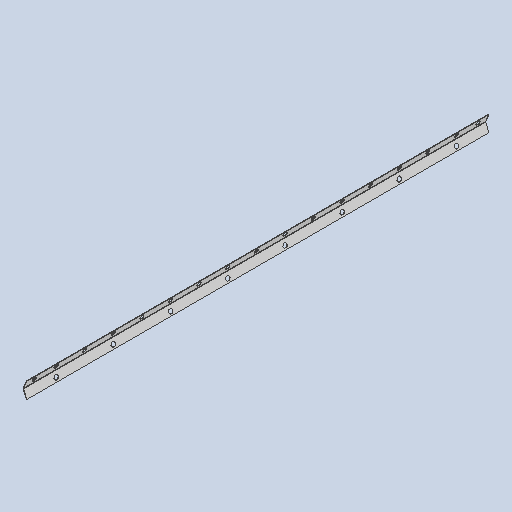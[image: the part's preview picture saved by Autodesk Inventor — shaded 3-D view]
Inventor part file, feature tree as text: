
AUTODESK INVENTOR PART (.ipt)
format: ipt  version: 2025 (Build 290162010, 162A)  size: 404,992 bytes
history: native  units: mm
features: sketch x4, sheet_metal_op x3, extrude x3, pattern_linear x2, other x2, mirror x1
ambient origin geometry x8: Origin, YZ Plane, XZ Plane, XY Plane, X Axis, Y Axis, Z Axis, Center Point
bodies: Body1 (feature_tree)
feature tree (15):
  sheet_metal_op  "Contour Flange1"
  extrude  "Extrusion1"  Depth=36.26mm
  extrude  "Extrusion6"  Depth=2.0mm
  mirror  "Mirror1"
  pattern_linear  "Rectangular Pattern4"  Spacing1=4.0mm  [1 undecoded]
  extrude  "Extrusion7"  Depth=2.0mm
  pattern_linear  "Rectangular Pattern5"  Count1=202  [1 undecoded]
  sketch  "Sketch4"  dims[d16=511.0mm d23=36.26mm]
  other  "Plate3"
  sheet_metal_op  "Bend2"
  sheet_metal_op  "Corner2"
  sketch  "Sketch6"  dims[d24=4.0mm d25=2.0mm]
  sketch  "Sketch12"  dims[d26=2.0mm]
  sketch  "Sketch13"  dims[d27=1.0mm d28=4.0mm d29=2.0mm d30=2020.0mm d31=2.0mm d32=3.0mm d33=8.0mm d34=2.0mm d35=2.0mm d36=11.0mm d41=11.0mm d42=10.0mm d43=0.0mm d75=50.0mm d76=25.0mm d77=125.0mm d78=0.0mm d79=0.0mm d80=80.0mm d82=250.0mm d83=11.0mm d84=0.0mm d85=0.0mm d86=70.0mm d88=250.0mm d93=19.22mm d94=40.75mm d95=19.22mm d96=40.75mm d97=16.8mm d98=16.8mm d99=16.8mm]
  other  "Definition1"
note: 2 required parameter values undecoded (feature->parameter linkage not recoverable at this tier; creation-order binding heuristic only, values carry confidence <= 0.55)
